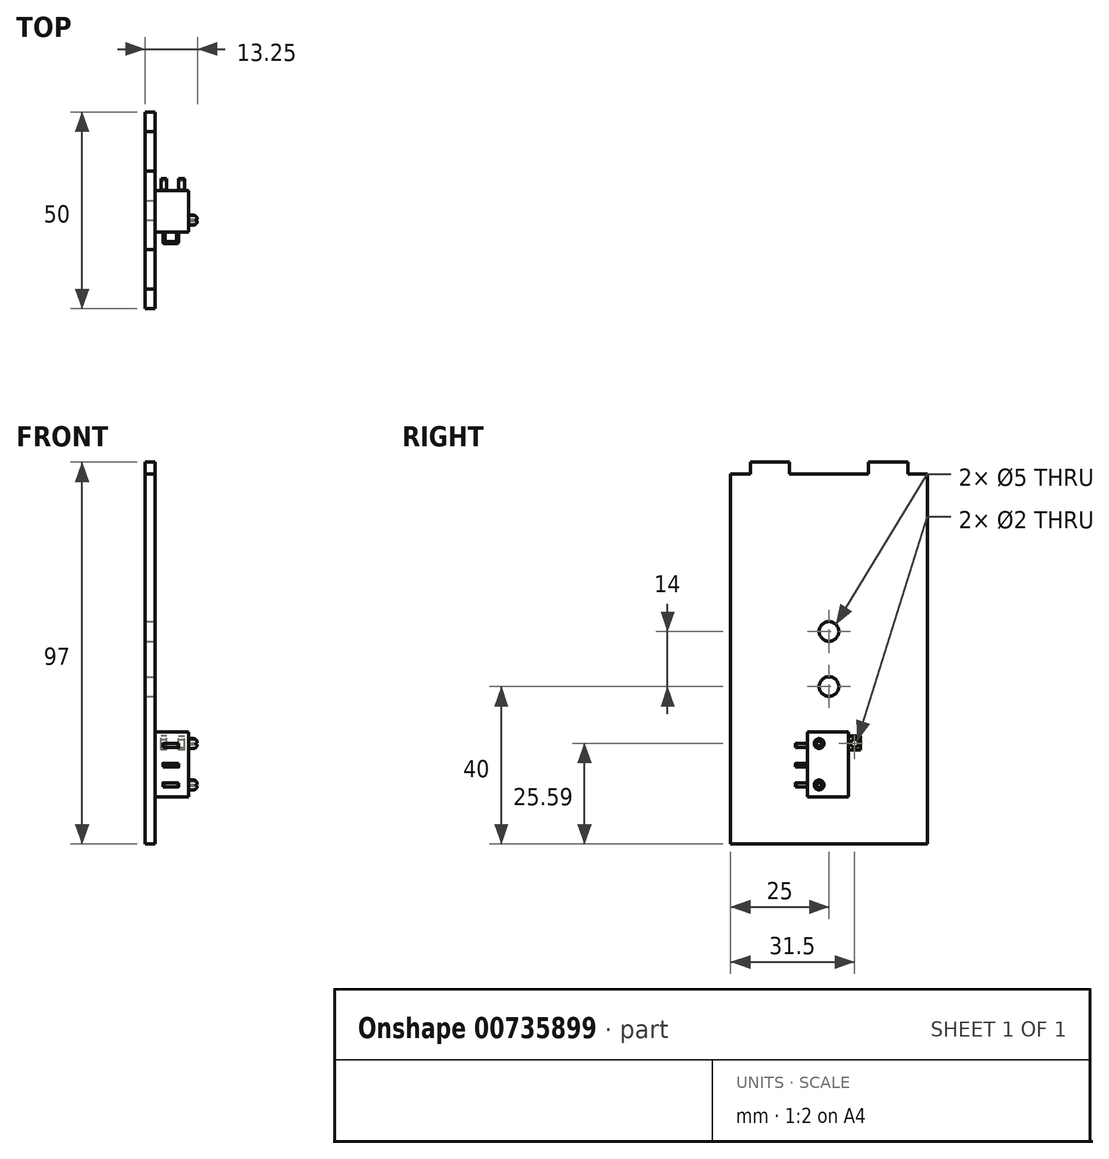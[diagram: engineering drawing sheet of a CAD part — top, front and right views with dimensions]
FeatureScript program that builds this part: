
annotation { "Feature Type Name" : "Feature", "Feature Type Description" : "" }
export const myFeature = defineFeature(function(context is Context, id is Id, definition is map)
    precondition{}
    {
        {
            var Q0;
            Q0=qCreatedBy(makeId("Right.planeOp"),FACE);
            var sketch = newSketch(context, id + "F0", { "sketchPlane" : qUnion([Q0])});
            skLineSegment(sketch, "E0.bottom", {"start": v(0, 0) * mm, "end": v(50, 0) * mm});
            skLineSegment(sketch, "E0.top", {"start": v(0, 94) * mm, "end": v(50, 94) * mm});
            skLineSegment(sketch, "E0.left", {"start": v(0, 0) * mm, "end": v(0, 94) * mm});
            skLineSegment(sketch, "E0.right", {"start": v(50, 0) * mm, "end": v(50, 94) * mm});
            skSolve(sketch);
        }
        {
            var Q0;
            Q0=makeQuery(id+"F0.imprint","IMPRINT",FACE,{"disambiguationData":[TD([[makeQuery(id+"F0.imprint","IMPRINT",EDGE,{"derivedFrom":sQuery(id+"F0.wireOp",EDGE,"E0.bottom")}),1.0]])]});
            extrude(context, id + "F1", {"entities" : qUnion([Q0]), "depth" : 2.5 * mm, "offsetDistance" : 25 * mm});
        }
        {
            var Q0;
            Q0=makeQuery(id+"F1.opExtrude","SWEPT_FACE",FACE,{"disambiguationData":[OSD([sQuery(id+"F0.wireOp",EDGE,"E0.top")])]});
            var sketch = newSketch(context, id + "F2", { "sketchPlane" : qUnion([Q0])});
            skLineSegment(sketch, "E1.bottom", {"start": v(2.5, 5) * mm, "end": v(0, 5) * mm});
            skLineSegment(sketch, "E1.top", {"start": v(2.5, 15) * mm, "end": v(0, 15) * mm});
            skLineSegment(sketch, "E1.left", {"start": v(2.5, 5) * mm, "end": v(2.5, 15) * mm});
            skLineSegment(sketch, "E1.right", {"start": v(0, 5) * mm, "end": v(0, 15) * mm});
            skLineSegment(sketch, "E2.bottom", {"start": v(2.5, 35) * mm, "end": v(0, 35) * mm});
            skLineSegment(sketch, "E2.top", {"start": v(2.5, 45) * mm, "end": v(0, 45) * mm});
            skLineSegment(sketch, "E2.left", {"start": v(2.5, 35) * mm, "end": v(2.5, 45) * mm});
            skLineSegment(sketch, "E2.right", {"start": v(0, 35) * mm, "end": v(0, 45) * mm});
            skSolve(sketch);
        }
        {
            var Q0;
            Q0=makeQuery(id+"F2.imprint","IMPRINT",FACE,{"disambiguationData":[TD([[makeQuery(id+"F2.imprint","IMPRINT",EDGE,{"derivedFrom":sQuery(id+"F2.wireOp",EDGE,"E2.bottom")}),-1.0]])]});
            var Q1;
            Q1=makeQuery(id+"F2.imprint","IMPRINT",FACE,{"disambiguationData":[TD([[makeQuery(id+"F2.imprint","IMPRINT",EDGE,{"derivedFrom":sQuery(id+"F2.wireOp",EDGE,"E1.bottom")}),-1.0]])]});
            extrude(context, id + "F3", {"entities" : qUnion([Q0, Q1]), "operationType" : NewBodyOperationType.ADD, "depth" : 3 * mm, "offsetDistance" : 25 * mm});
        }
        {
            var Q0;
            Q0=makeQuery(id+"F3.boolean.opBoolean","MERGE",FACE,{"derivedFrom":[makeQuery(id+"F1.opExtrude","CAP_FACE",FACE,{"disambiguationData":[OSD([sQuery(id+"F0.wireOp",EDGE,"E0.bottom"),sQuery(id+"F0.wireOp",EDGE,"E0.top"),sQuery(id+"F0.wireOp",EDGE,"E0.left"),sQuery(id+"F0.wireOp",EDGE,"E0.right")])],"isStart":false}),makeQuery(id+"F3.opExtrude","SWEPT_FACE",FACE,{"disambiguationData":[OSD([sQuery(id+"F2.wireOp",EDGE,"E1.left")])]}),makeQuery(id+"F3.opExtrude","SWEPT_FACE",FACE,{"disambiguationData":[OSD([sQuery(id+"F2.wireOp",EDGE,"E2.left")])]})]});
            var sketch = newSketch(context, id + "F4", { "sketchPlane" : qUnion([Q0])});
            skCircle(sketch, "E3", {"center": v(25, 54) * mm, "radius": 2.5 * mm});
            skCircle(sketch, "E4", {"center": v(25, 40) * mm, "radius": 2.5 * mm});
            skSolve(sketch);
        }
        {
            var Q0;
            Q0=makeQuery(id+"F4.imprint","IMPRINT",FACE,{"disambiguationData":[TD([[makeQuery(id+"F4.imprint","IMPRINT",EDGE,{"derivedFrom":sQuery(id+"F4.wireOp",EDGE,"E4")}),1.0]])]});
            var Q1;
            Q1=makeQuery(id+"F4.imprint","IMPRINT",FACE,{"disambiguationData":[TD([[makeQuery(id+"F4.imprint","IMPRINT",EDGE,{"derivedFrom":sQuery(id+"F4.wireOp",EDGE,"E3")}),1.0]])]});
            extrude(context, id + "F5", {"entities" : qUnion([Q0, Q1]), "operationType" : NewBodyOperationType.REMOVE, "oppositeDirection" : true, "depth" : 25 * mm, "offsetDistance" : 25 * mm});
        }
        {
            var Q0;
            Q0=makeQuery(id+"F3.boolean.opBoolean","MERGE",FACE,{"derivedFrom":[makeQuery(id+"F1.opExtrude","CAP_FACE",FACE,{"disambiguationData":[OSD([sQuery(id+"F0.wireOp",EDGE,"E0.bottom"),sQuery(id+"F0.wireOp",EDGE,"E0.top"),sQuery(id+"F0.wireOp",EDGE,"E0.left"),sQuery(id+"F0.wireOp",EDGE,"E0.right")])],"isStart":false}),makeQuery(id+"F3.opExtrude","SWEPT_FACE",FACE,{"disambiguationData":[OSD([sQuery(id+"F2.wireOp",EDGE,"E1.left")])]}),makeQuery(id+"F3.opExtrude","SWEPT_FACE",FACE,{"disambiguationData":[OSD([sQuery(id+"F2.wireOp",EDGE,"E2.left")])]})]});
            var sketch = newSketch(context, id + "F6", { "sketchPlane" : qUnion([Q0])});
            skLineSegment(sketch, "E5.bottom", {"start": v(19.5, 28.52) * mm, "end": v(30, 28.52) * mm});
            skLineSegment(sketch, "E5.top", {"start": v(19.5, 12) * mm, "end": v(30, 12) * mm});
            skLineSegment(sketch, "E5.left", {"start": v(19.5, 28.52) * mm, "end": v(19.5, 12) * mm});
            skLineSegment(sketch, "E5.right", {"start": v(30, 28.52) * mm, "end": v(30, 12) * mm});
            skSolve(sketch);
        }
        {
            var Q0;
            Q0=makeQuery(id+"F6.imprint","IMPRINT",FACE,{"disambiguationData":[TD([[makeQuery(id+"F6.imprint","IMPRINT",EDGE,{"derivedFrom":sQuery(id+"F6.wireOp",EDGE,"E5.bottom")}),-1.0]])]});
            extrude(context, id + "F7", {"entities" : qUnion([Q0]), "operationType" : NewBodyOperationType.ADD, "depth" : 8.5 * mm, "offsetDistance" : 25 * mm});
        }
        {
            var Q0;
            Q0=makeQuery(id+"F7.opExtrude","SWEPT_FACE",FACE,{"disambiguationData":[OSD([sQuery(id+"F6.wireOp",EDGE,"E5.left")])]});
            var sketch = newSketch(context, id + "F8", { "sketchPlane" : qUnion([Q0])});
            skLineSegment(sketch, "E6.bottom", {"start": v(4.5, 24.52) * mm, "end": v(8.5, 24.52) * mm});
            skLineSegment(sketch, "E6.top", {"start": v(4.5, 25.52) * mm, "end": v(8.5, 25.52) * mm});
            skLineSegment(sketch, "E6.left", {"start": v(4.5, 24.52) * mm, "end": v(4.5, 25.52) * mm});
            skLineSegment(sketch, "E6.right", {"start": v(8.5, 24.52) * mm, "end": v(8.5, 25.52) * mm});
            skLineSegment(sketch, "E7.bottom", {"start": v(4.5, 19.52) * mm, "end": v(8.5, 19.52) * mm});
            skLineSegment(sketch, "E7.top", {"start": v(4.5, 20.52) * mm, "end": v(8.5, 20.52) * mm});
            skLineSegment(sketch, "E7.left", {"start": v(4.5, 19.52) * mm, "end": v(4.5, 20.52) * mm});
            skLineSegment(sketch, "E7.right", {"start": v(8.5, 19.52) * mm, "end": v(8.5, 20.52) * mm});
            skLineSegment(sketch, "E8.bottom", {"start": v(4.5, 14.52) * mm, "end": v(8.5, 14.52) * mm});
            skLineSegment(sketch, "E8.top", {"start": v(4.5, 15.52) * mm, "end": v(8.5, 15.52) * mm});
            skLineSegment(sketch, "E8.left", {"start": v(4.5, 14.52) * mm, "end": v(4.5, 15.52) * mm});
            skLineSegment(sketch, "E8.right", {"start": v(8.5, 14.52) * mm, "end": v(8.5, 15.52) * mm});
            skSolve(sketch);
        }
        {
            var Q0;
            Q0=makeQuery(id+"F8.imprint","IMPRINT",FACE,{"disambiguationData":[TD([[makeQuery(id+"F8.imprint","IMPRINT",EDGE,{"derivedFrom":sQuery(id+"F8.wireOp",EDGE,"E6.bottom")}),1.0]])]});
            var Q1;
            Q1=makeQuery(id+"F8.imprint","IMPRINT",FACE,{"disambiguationData":[TD([[makeQuery(id+"F8.imprint","IMPRINT",EDGE,{"derivedFrom":sQuery(id+"F8.wireOp",EDGE,"E7.bottom")}),1.0]])]});
            var Q2;
            Q2=makeQuery(id+"F8.imprint","IMPRINT",FACE,{"disambiguationData":[TD([[makeQuery(id+"F8.imprint","IMPRINT",EDGE,{"derivedFrom":sQuery(id+"F8.wireOp",EDGE,"E8.bottom")}),1.0]])]});
            extrude(context, id + "F9", {"entities" : qUnion([Q0, Q1, Q2]), "operationType" : NewBodyOperationType.ADD, "depth" : 3 * mm, "offsetDistance" : 25 * mm});
        }
        {
            var Q0;
            Q0=makeQuery(id+"F9.opExtrude","SWEPT_FACE",FACE,{"disambiguationData":[OSD([sQuery(id+"F8.wireOp",EDGE,"E8.bottom")])]});
            var sketch = newSketch(context, id + "F10", { "sketchPlane" : qUnion([Q0])});
            skLineSegment(sketch, "E9.bottom", {"start": v(5, -19.5) * mm, "end": v(8, -19.5) * mm});
            skLineSegment(sketch, "E9.top", {"start": v(5.5, -17) * mm, "end": v(7.5, -17) * mm});
            skLineSegment(sketch, "E9.left", {"start": v(5, -19.5) * mm, "end": v(5, -17.5) * mm});
            skLineSegment(sketch, "E9.right", {"start": v(8, -19.5) * mm, "end": v(8, -17.5) * mm});
            skPoint(sketch, "E10.visualSharp", {"position": v(8, -17) * mm});
            skArc(sketch, "E10.filletArc", {"start": v(8, -17.5) * mm, "mid": v(7.85, -17.15) * mm, "end": v(7.5, -17) * mm});
            skPoint(sketch, "E11.visualSharp", {"position": v(5, -17) * mm});
            skArc(sketch, "E11.filletArc", {"start": v(5.5, -17) * mm, "mid": v(5.15, -17.15) * mm, "end": v(5, -17.5) * mm});
            skSolve(sketch);
        }
        {
            var Q0;
            Q0=makeQuery(id+"F10.imprint","IMPRINT",FACE,{"disambiguationData":[TD([[makeQuery(id+"F10.imprint","IMPRINT",EDGE,{"derivedFrom":sQuery(id+"F10.wireOp",EDGE,"E9.bottom")}),1.0]])]});
            extrude(context, id + "F11", {"entities" : qUnion([Q0]), "operationType" : NewBodyOperationType.REMOVE, "endBound" : BoundingType.THROUGH_ALL, "oppositeDirection" : true, "depth" : 25 * mm, "offsetDistance" : 25 * mm});
        }
        {
            var Q0;
            Q0=makeQuery(id+"F9.opExtrude","CAP_EDGE",EDGE,{"disambiguationData":[OSD([sQuery(id+"F8.wireOp",EDGE,"E8.right")])],"isStart":false});
            var Q1;
            Q1=makeQuery(id+"F9.opExtrude","CAP_EDGE",EDGE,{"disambiguationData":[OSD([sQuery(id+"F8.wireOp",EDGE,"E7.right")])],"isStart":false});
            var Q2;
            Q2=makeQuery(id+"F9.opExtrude","CAP_EDGE",EDGE,{"disambiguationData":[OSD([sQuery(id+"F8.wireOp",EDGE,"E6.right")])],"isStart":false});
            var Q3;
            Q3=makeQuery(id+"F9.opExtrude","CAP_EDGE",EDGE,{"disambiguationData":[OSD([sQuery(id+"F8.wireOp",EDGE,"E6.left")])],"isStart":false});
            var Q4;
            Q4=makeQuery(id+"F9.opExtrude","CAP_EDGE",EDGE,{"disambiguationData":[OSD([sQuery(id+"F8.wireOp",EDGE,"E7.left")])],"isStart":false});
            var Q5;
            Q5=makeQuery(id+"F9.opExtrude","CAP_EDGE",EDGE,{"disambiguationData":[OSD([sQuery(id+"F8.wireOp",EDGE,"E8.left")])],"isStart":false});
            fillet(context, id + "F12", {"entities" : qUnion([Q0, Q1, Q2, Q3, Q4, Q5]), "radius" : .5 * mm, "tangentPropagation" : true, "allowEdgeOverflow" : false});
        }
        {
            var Q0;
            Q0=makeQuery(id+"F7.opExtrude","CAP_FACE",FACE,{"disambiguationData":[OSD([sQuery(id+"F6.wireOp",EDGE,"E5.bottom"),sQuery(id+"F6.wireOp",EDGE,"E5.top"),sQuery(id+"F6.wireOp",EDGE,"E5.left"),sQuery(id+"F6.wireOp",EDGE,"E5.right")])],"isStart":false});
            var sketch = newSketch(context, id + "F13", { "sketchPlane" : qUnion([Q0])});
            skCircle(sketch, "E12", {"center": v(22.5, 25.52) * mm, "radius": 1.25 * mm});
            skCircle(sketch, "E13", {"center": v(22.5, 15) * mm, "radius": 1.25 * mm});
            skSolve(sketch);
        }
        {
            var Q0;
            Q0=makeQuery(id+"F13.imprint","IMPRINT",FACE,{"disambiguationData":[TD([[makeQuery(id+"F13.imprint","IMPRINT",EDGE,{"derivedFrom":sQuery(id+"F13.wireOp",EDGE,"E12")}),1.0]])]});
            var Q1;
            Q1=makeQuery(id+"F13.imprint","IMPRINT",FACE,{"disambiguationData":[TD([[makeQuery(id+"F13.imprint","IMPRINT",EDGE,{"derivedFrom":sQuery(id+"F13.wireOp",EDGE,"E13")}),1.0]])]});
            extrude(context, id + "F14", {"entities" : qUnion([Q0, Q1]), "operationType" : NewBodyOperationType.ADD, "depth" : 2.25 * mm, "offsetDistance" : 25 * mm});
        }
        {
            var Q0;
            Q0=makeQuery(id+"F14.opExtrude","CAP_FACE",FACE,{"disambiguationData":[OSD([sQuery(id+"F13.wireOp",EDGE,"E12")])],"isStart":false});
            var sketch = newSketch(context, id + "F15", { "sketchPlane" : qUnion([Q0])});
            skLineSegment(sketch, "E14.bottom", {"start": v(22.25, 24.58) * mm, "end": v(22.75, 24.58) * mm});
            skLineSegment(sketch, "E14.top", {"start": v(22.25, 26.43) * mm, "end": v(22.75, 26.43) * mm});
            skLineSegment(sketch, "E14.left", {"start": v(22.25, 24.58) * mm, "end": v(22.25, 25.3) * mm});
            skLineSegment(sketch, "E14.right", {"start": v(22.75, 24.58) * mm, "end": v(22.75, 25.3) * mm});
            skLineSegment(sketch, "E15.bottom", {"start": v(21.56, 25.73) * mm, "end": v(22.25, 25.73) * mm});
            skLineSegment(sketch, "E15.top", {"start": v(21.56, 25.3) * mm, "end": v(22.25, 25.3) * mm});
            skLineSegment(sketch, "E15.left", {"start": v(21.56, 25.73) * mm, "end": v(21.56, 25.3) * mm});
            skLineSegment(sketch, "E15.right", {"start": v(23.52, 25.73) * mm, "end": v(23.52, 25.3) * mm});
            skLineSegment(sketch, "E16.trimOffspring", {"start": v(22.75, 25.73) * mm, "end": v(23.52, 25.73) * mm});
            skLineSegment(sketch, "E17.trimOffspring", {"start": v(22.75, 25.73) * mm, "end": v(22.75, 26.43) * mm});
            skLineSegment(sketch, "E18.trimOffspring", {"start": v(22.75, 25.3) * mm, "end": v(23.52, 25.3) * mm});
            skLineSegment(sketch, "E19.trimOffspring", {"start": v(22.25, 25.73) * mm, "end": v(22.25, 26.43) * mm});
            skLineSegment(sketch, "E20.bottom", {"start": v(22.26, 14.04) * mm, "end": v(22.76, 14.04) * mm});
            skLineSegment(sketch, "E20.top", {"start": v(22.26, 15.9) * mm, "end": v(22.76, 15.9) * mm});
            skLineSegment(sketch, "E20.left", {"start": v(22.26, 14.04) * mm, "end": v(22.26, 14.76) * mm});
            skLineSegment(sketch, "E20.right", {"start": v(22.76, 14.04) * mm, "end": v(22.76, 14.76) * mm});
            skLineSegment(sketch, "E21.bottom", {"start": v(21.57, 15.2) * mm, "end": v(22.26, 15.2) * mm});
            skLineSegment(sketch, "E21.top", {"start": v(21.57, 14.76) * mm, "end": v(22.26, 14.76) * mm});
            skLineSegment(sketch, "E21.left", {"start": v(21.57, 15.2) * mm, "end": v(21.57, 14.76) * mm});
            skLineSegment(sketch, "E21.right", {"start": v(23.52, 15.2) * mm, "end": v(23.52, 14.76) * mm});
            skLineSegment(sketch, "E22.trimOffspring", {"start": v(22.76, 15.2) * mm, "end": v(22.76, 15.9) * mm});
            skLineSegment(sketch, "E23.trimOffspring", {"start": v(22.76, 14.76) * mm, "end": v(23.52, 14.76) * mm});
            skLineSegment(sketch, "E24.trimOffspring", {"start": v(22.26, 15.2) * mm, "end": v(22.26, 15.9) * mm});
            skLineSegment(sketch, "E25", {"start": v(22.76, 15.2) * mm, "end": v(23.52, 15.2) * mm});
            skSolve(sketch);
        }
        {
            var Q0;
            Q0 = qSketchRegion(id + "F15", true);
            extrude(context, id + "F16", {"entities" : qUnion([Q0]), "operationType" : NewBodyOperationType.REMOVE, "oppositeDirection" : true, "depth" : 2 * mm, "offsetDistance" : 25 * mm});
        }
        {
            var Q0;
            Q0=makeQuery(id+"F14.opExtrude","CAP_EDGE",EDGE,{"disambiguationData":[OSD([sQuery(id+"F13.wireOp",EDGE,"E12")])],"isStart":false});
            var Q1;
            Q1=makeQuery(id+"F14.opExtrude","CAP_EDGE",EDGE,{"disambiguationData":[OSD([sQuery(id+"F13.wireOp",EDGE,"E13")])],"isStart":false});
            fillet(context, id + "F17", {"entities" : qUnion([Q0, Q1]), "radius" : 1 * mm, "tangentPropagation" : true, "allowEdgeOverflow" : false});
        }
        {
            var Q0;
            Q0=makeQuery(id+"F7.opExtrude","SWEPT_FACE",FACE,{"disambiguationData":[OSD([sQuery(id+"F6.wireOp",EDGE,"E5.right")])]});
            var sketch = newSketch(context, id + "F18", { "sketchPlane" : qUnion([Q0])});
            skLineSegment(sketch, "E26.bottom", {"start": v(-10, 23.84) * mm, "end": v(-8.5, 23.84) * mm});
            skLineSegment(sketch, "E26.top", {"start": v(-10, 27.34) * mm, "end": v(-8.5, 27.34) * mm});
            skLineSegment(sketch, "E26.left", {"start": v(-10, 23.84) * mm, "end": v(-10, 27.34) * mm});
            skLineSegment(sketch, "E26.right", {"start": v(-8.5, 23.84) * mm, "end": v(-8.5, 27.34) * mm});
            skLineSegment(sketch, "E27.bottom", {"start": v(-5.5, 23.91) * mm, "end": v(-4, 23.91) * mm});
            skLineSegment(sketch, "E27.top", {"start": v(-5.5, 27.41) * mm, "end": v(-4, 27.41) * mm});
            skLineSegment(sketch, "E27.left", {"start": v(-5.5, 23.91) * mm, "end": v(-5.5, 27.41) * mm});
            skLineSegment(sketch, "E27.right", {"start": v(-4, 23.91) * mm, "end": v(-4, 27.41) * mm});
            skSolve(sketch);
        }
        {
            var Q0;
            Q0=makeQuery(id+"F18.imprint","IMPRINT",FACE,{"disambiguationData":[TD([[makeQuery(id+"F18.imprint","IMPRINT",EDGE,{"derivedFrom":sQuery(id+"F18.wireOp",EDGE,"E26.bottom")}),1.0]])]});
            var Q1;
            Q1=makeQuery(id+"F18.imprint","IMPRINT",FACE,{"disambiguationData":[TD([[makeQuery(id+"F18.imprint","IMPRINT",EDGE,{"derivedFrom":sQuery(id+"F18.wireOp",EDGE,"E27.bottom")}),1.0]])]});
            extrude(context, id + "F19", {"entities" : qUnion([Q0, Q1]), "operationType" : NewBodyOperationType.ADD, "depth" : 3 * mm, "offsetDistance" : 25 * mm});
        }
        {
            var Q0;
            Q0=makeQuery(id+"F19.opExtrude","SWEPT_FACE",FACE,{"disambiguationData":[OSD([sQuery(id+"F18.wireOp",EDGE,"E26.left")])]});
            var sketch = newSketch(context, id + "F20", { "sketchPlane" : qUnion([Q0])});
            skCircle(sketch, "E28", {"center": v(31.5, 25.6) * mm, "radius": 1 * mm});
            skSolve(sketch);
        }
        {
            var Q0;
            Q0=makeQuery(id+"F20.imprint","IMPRINT",FACE,{"disambiguationData":[TD([[makeQuery(id+"F20.imprint","IMPRINT",EDGE,{"derivedFrom":sQuery(id+"F20.wireOp",EDGE,"E28")}),1.0]])]});
            extrude(context, id + "F21", {"entities" : qUnion([Q0]), "operationType" : NewBodyOperationType.REMOVE, "oppositeDirection" : true, "depth" : 6 * mm, "offsetDistance" : 25 * mm});
        }
    });
